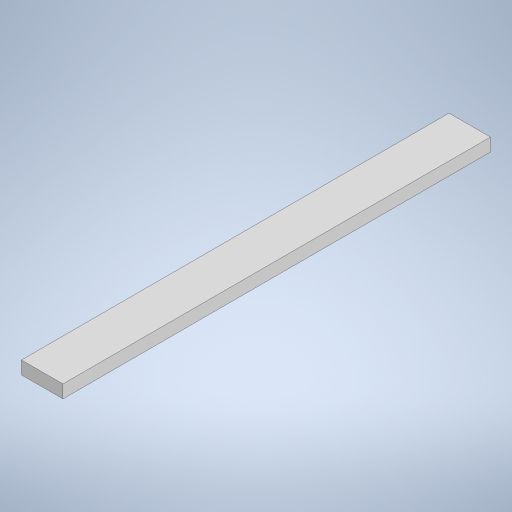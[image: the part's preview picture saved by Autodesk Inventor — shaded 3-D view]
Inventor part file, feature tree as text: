
AUTODESK INVENTOR PART (.ipt)
format: ipt  version: 2024 (Build 280153000, 153)  size: 224,256 bytes
history: native  units: mm
features: extrude x1, sketch x1
ambient origin geometry x8: Origin, YZ Plane, XZ Plane, XY Plane, X Axis, Y Axis, Z Axis, Center Point
bodies: Solid1 (feature_tree)
feature tree (2):
  extrude  "Extrusion1"  Depth=103.0mm
  sketch  "Sketch1"  dims[d0=10.0mm d1=103.0mm d2=3.125mm d3=0.0mm]
